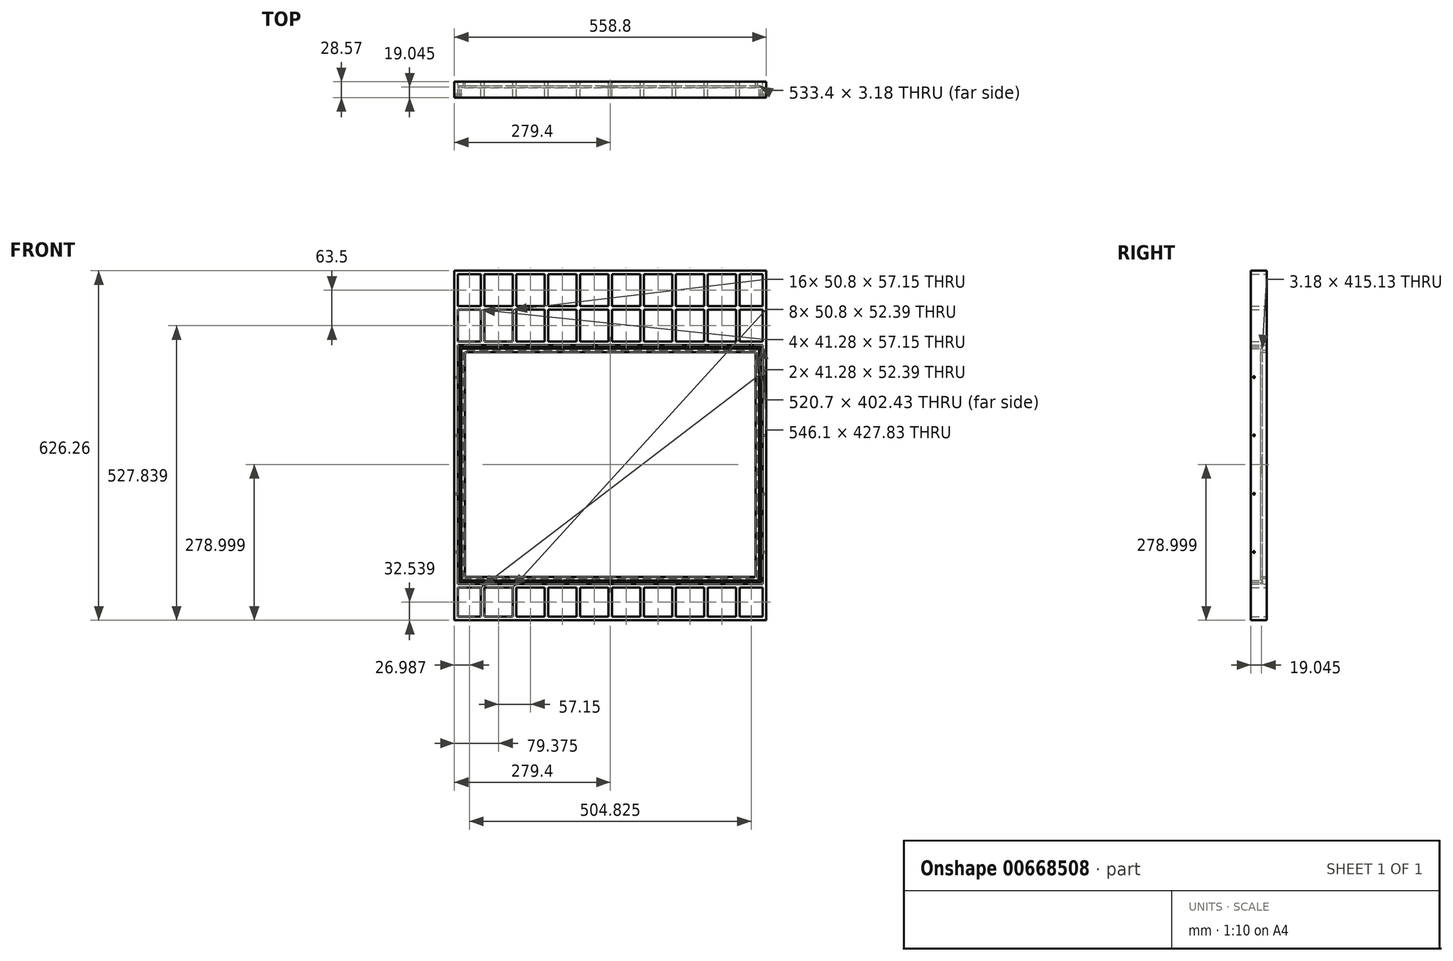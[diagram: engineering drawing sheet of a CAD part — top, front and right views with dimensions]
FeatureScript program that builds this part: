
annotation { "Feature Type Name" : "Feature", "Feature Type Description" : "" }
export const myFeature = defineFeature(function(context is Context, id is Id, definition is map)
    precondition{}
    {
        {
            var Q0;
            Q0=qCreatedBy(makeId("Front.planeOp"),FACE);
            var sketch = newSketch(context, id + "F0", { "sketchPlane" : qUnion([Q0])});
            skLineSegment(sketch, "E0.bottom", {"start": v(-279.4, -313.13) * mm, "end": v(279.4, -313.13) * mm});
            skLineSegment(sketch, "E0.top", {"start": v(-279.4, 313.13) * mm, "end": v(279.4, 313.13) * mm});
            skLineSegment(sketch, "E0.left", {"start": v(-279.4, -313.13) * mm, "end": v(-279.4, 313.13) * mm});
            skLineSegment(sketch, "E0.right", {"start": v(279.4, -313.13) * mm, "end": v(279.4, 313.13) * mm});
            skPoint(sketch, "E0.middle", {"position": v(0, 0) * mm});
            skLineSegment(sketch, "E1.0", {"start": v(-273.05, 179.78) * mm, "end": v(273.05, 179.78) * mm});
            skLineSegment(sketch, "E2", {"start": v(-409.08, -332.18) * mm, "end": v(546.13, -332.18) * mm, "construction": true});
            skLineSegment(sketch, "E3.0", {"start": v(-409.08, -351.23) * mm, "end": v(546.13, -351.23) * mm});
            skLineSegment(sketch, "E4", {"start": v(-273.05, -248.05) * mm, "end": v(273.05, -248.05) * mm});
            skLineSegment(sketch, "E5.0", {"start": v(-273.05, -306.78) * mm, "end": v(-273.05, 306.78) * mm});
            skLineSegment(sketch, "E5.1", {"start": v(-273.05, -306.78) * mm, "end": v(273.05, -306.78) * mm});
            skLineSegment(sketch, "E5.2", {"start": v(273.05, -306.78) * mm, "end": v(273.05, 306.78) * mm});
            skLineSegment(sketch, "E5.3", {"start": v(-273.05, 306.78) * mm, "end": v(273.05, 306.78) * mm});
            skLineSegment(sketch, "E6.0", {"start": v(-273.05, 186.13) * mm, "end": v(273.05, 186.13) * mm});
            skLineSegment(sketch, "E7", {"start": v(-291.57, 348.06) * mm, "end": v(292.45, 348.06) * mm, "construction": true});
            skLineSegment(sketch, "E8.0", {"start": v(-273.05, -254.4) * mm, "end": v(273.05, -254.4) * mm});
            skLineSegment(sketch, "E9", {"start": v(0, 186.13) * mm, "end": v(0, 306.78) * mm, "construction": true});
            skLineSegment(sketch, "E10", {"start": v(53.97, 306.78) * mm, "end": v(53.98, 186.13) * mm});
            skLineSegment(sketch, "E11", {"start": v(111.13, 306.78) * mm, "end": v(111.13, 186.13) * mm});
            skLineSegment(sketch, "E12", {"start": v(168.28, 306.78) * mm, "end": v(168.28, 186.13) * mm});
            skLineSegment(sketch, "E13.0", {"start": v(3.18, 186.13) * mm, "end": v(3.18, 306.78) * mm});
            skLineSegment(sketch, "E14.0", {"start": v(60.33, 306.78) * mm, "end": v(60.33, 186.13) * mm});
            skLineSegment(sketch, "E15", {"start": v(117.48, 306.78) * mm, "end": v(117.48, 186.13) * mm});
            skLineSegment(sketch, "E16", {"start": v(174.63, 306.78) * mm, "end": v(174.63, 186.13) * mm});
            skLineSegment(sketch, "E17.0", {"start": v(225.43, 306.78) * mm, "end": v(225.43, 186.13) * mm});
            skLineSegment(sketch, "E18.0", {"start": v(231.78, 313.13) * mm, "end": v(231.78, 186.13) * mm});
            skLineSegment(sketch, "E19.0", {"start": v(-3.18, 186.13) * mm, "end": v(-3.18, 306.78) * mm});
            skLineSegment(sketch, "E20.0", {"start": v(-53.98, 186.13) * mm, "end": v(-53.98, 306.78) * mm});
            skLineSegment(sketch, "E21.0", {"start": v(-60.33, 186.13) * mm, "end": v(-60.33, 306.78) * mm});
            skLineSegment(sketch, "E22.0", {"start": v(-111.12, 186.13) * mm, "end": v(-111.12, 306.78) * mm});
            skLineSegment(sketch, "E23.0", {"start": v(-117.47, 186.13) * mm, "end": v(-117.47, 306.78) * mm});
            skLineSegment(sketch, "E24.0", {"start": v(-168.28, 186.13) * mm, "end": v(-168.28, 306.78) * mm});
            skLineSegment(sketch, "E25.0", {"start": v(-174.62, 186.13) * mm, "end": v(-174.62, 306.78) * mm});
            skLineSegment(sketch, "E26.0", {"start": v(-225.42, 186.13) * mm, "end": v(-225.42, 306.78) * mm});
            skLineSegment(sketch, "E27.0", {"start": v(-231.78, 186.13) * mm, "end": v(-231.78, 306.78) * mm});
            skPoint(sketch, "E28.endSnap0", {"position": v(231.78, 249.63) * mm});
            skLineSegment(sketch, "E29", {"start": v(0, 246.46) * mm, "end": v(-273.05, 246.46) * mm, "construction": true});
            skLineSegment(sketch, "E30.0", {"start": v(273.05, 249.63) * mm, "end": v(-273.05, 249.63) * mm});
            skLineSegment(sketch, "E31.0", {"start": v(273.05, 243.28) * mm, "end": v(-273.05, 243.28) * mm});
            skLineSegment(sketch, "E32", {"start": v(-231.78, -248.05) * mm, "end": v(-231.78, -306.78) * mm});
            skLineSegment(sketch, "E33.0", {"start": v(-225.43, -254.4) * mm, "end": v(-225.43, -306.78) * mm});
            skLineSegment(sketch, "E34.0", {"start": v(-174.63, -254.4) * mm, "end": v(-174.63, -306.78) * mm});
            skLineSegment(sketch, "E35.0", {"start": v(-168.28, -254.4) * mm, "end": v(-168.28, -306.78) * mm});
            skLineSegment(sketch, "E36", {"start": v(-117.48, -254.4) * mm, "end": v(-117.48, -306.78) * mm});
            skLineSegment(sketch, "E37", {"start": v(-111.13, -254.4) * mm, "end": v(-111.13, -306.78) * mm});
            skLineSegment(sketch, "E38", {"start": v(-60.33, -254.4) * mm, "end": v(-60.33, -306.78) * mm});
            skLineSegment(sketch, "E39", {"start": v(-53.98, -254.4) * mm, "end": v(-53.98, -306.78) * mm});
            skLineSegment(sketch, "E40", {"start": v(-3.18, -254.4) * mm, "end": v(-3.18, -306.78) * mm});
            skLineSegment(sketch, "E41", {"start": v(3.17, -254.4) * mm, "end": v(3.17, -306.78) * mm});
            skLineSegment(sketch, "E42", {"start": v(53.97, -254.4) * mm, "end": v(53.97, -306.78) * mm});
            skLineSegment(sketch, "E43", {"start": v(60.32, -254.4) * mm, "end": v(60.32, -306.78) * mm});
            skLineSegment(sketch, "E44", {"start": v(111.12, -254.4) * mm, "end": v(111.12, -306.78) * mm});
            skLineSegment(sketch, "E45", {"start": v(117.47, -254.4) * mm, "end": v(117.47, -306.78) * mm});
            skLineSegment(sketch, "E46", {"start": v(168.27, -254.4) * mm, "end": v(168.27, -306.78) * mm});
            skLineSegment(sketch, "E47", {"start": v(174.62, -254.4) * mm, "end": v(174.62, -306.78) * mm});
            skLineSegment(sketch, "E48", {"start": v(225.42, -254.4) * mm, "end": v(225.42, -306.78) * mm});
            skLineSegment(sketch, "E49", {"start": v(231.77, -254.4) * mm, "end": v(231.77, -306.78) * mm});
            skSolve(sketch);
        }
        {
            var Q0;
            Q0 = qSketchRegion(id + "F0", true);
            var Q1;
            {var subQ0=sQuery(id+"F0.wireOp",EDGE,"E26.0");var subQ1=sQuery(id+"F0.wireOp",EDGE,"E5.3");var subQ2=makeQuery(id+"F0.imprint","INTERSECT",VERTEX,{"derivedFrom":[subQ1,subQ0]});Q1=makeQuery(id+"F0.imprint","IMPRINT",FACE,{"disambiguationData":[TD([[makeQuery(id+"F0.imprint","IMPRINT",EDGE,{"disambiguationData":[TD([[subQ2,1.0]])],"derivedFrom":subQ1}),-1.0]])]});}
            var Q2;
            {var subQ0=sQuery(id+"F0.wireOp",EDGE,"E31.0");var subQ1=sQuery(id+"F0.wireOp",EDGE,"E26.0");var subQ2=makeQuery(id+"F0.imprint","INTERSECT",VERTEX,{"derivedFrom":[subQ1,subQ0]});Q2=makeQuery(id+"F0.imprint","IMPRINT",FACE,{"disambiguationData":[TD([[makeQuery(id+"F0.imprint","IMPRINT",EDGE,{"disambiguationData":[TD([[subQ2,-1.0]])],"derivedFrom":subQ1}),1.0]])]});}
            var Q3;
            {var subQ0=sQuery(id+"F0.wireOp",EDGE,"E30.0");var subQ1=sQuery(id+"F0.wireOp",EDGE,"E5.0");var subQ2=makeQuery(id+"F0.imprint","INTERSECT",VERTEX,{"derivedFrom":[subQ1,subQ0]});Q3=makeQuery(id+"F0.imprint","IMPRINT",FACE,{"disambiguationData":[TD([[makeQuery(id+"F0.imprint","IMPRINT",EDGE,{"disambiguationData":[TD([[subQ2,1.0]])],"derivedFrom":subQ1}),-1.0]])]});}
            var Q4;
            {var subQ0=sQuery(id+"F0.wireOp",EDGE,"E26.0");var subQ1=sQuery(id+"F0.wireOp",EDGE,"E6.0");var subQ2=makeQuery(id+"F0.imprint","INTERSECT",VERTEX,{"derivedFrom":[subQ1,subQ0]});Q4=makeQuery(id+"F0.imprint","IMPRINT",FACE,{"disambiguationData":[TD([[makeQuery(id+"F0.imprint","IMPRINT",EDGE,{"disambiguationData":[TD([[subQ2,1.0]])],"derivedFrom":subQ1}),1.0]])]});}
            var Q5;
            {var subQ0=sQuery(id+"F0.wireOp",EDGE,"E31.0");var subQ1=sQuery(id+"F0.wireOp",EDGE,"E25.0");var subQ2=makeQuery(id+"F0.imprint","INTERSECT",VERTEX,{"derivedFrom":[subQ1,subQ0]});Q5=makeQuery(id+"F0.imprint","IMPRINT",FACE,{"disambiguationData":[TD([[makeQuery(id+"F0.imprint","IMPRINT",EDGE,{"disambiguationData":[TD([[subQ2,-1.0]])],"derivedFrom":subQ1}),1.0]])]});}
            var Q6;
            {var subQ0=sQuery(id+"F0.wireOp",EDGE,"E31.0");var subQ1=sQuery(id+"F0.wireOp",EDGE,"E24.0");var subQ2=makeQuery(id+"F0.imprint","INTERSECT",VERTEX,{"derivedFrom":[subQ1,subQ0]});Q6=makeQuery(id+"F0.imprint","IMPRINT",FACE,{"disambiguationData":[TD([[makeQuery(id+"F0.imprint","IMPRINT",EDGE,{"disambiguationData":[TD([[subQ2,-1.0]])],"derivedFrom":subQ1}),1.0]])]});}
            var Q7;
            {var subQ0=sQuery(id+"F0.wireOp",EDGE,"E24.0");var subQ1=sQuery(id+"F0.wireOp",EDGE,"E5.3");var subQ2=makeQuery(id+"F0.imprint","INTERSECT",VERTEX,{"derivedFrom":[subQ1,subQ0]});Q7=makeQuery(id+"F0.imprint","IMPRINT",FACE,{"disambiguationData":[TD([[makeQuery(id+"F0.imprint","IMPRINT",EDGE,{"disambiguationData":[TD([[subQ2,1.0]])],"derivedFrom":subQ1}),-1.0]])]});}
            var Q8;
            {var subQ0=sQuery(id+"F0.wireOp",EDGE,"E24.0");var subQ1=sQuery(id+"F0.wireOp",EDGE,"E6.0");var subQ2=makeQuery(id+"F0.imprint","INTERSECT",VERTEX,{"derivedFrom":[subQ1,subQ0]});Q8=makeQuery(id+"F0.imprint","IMPRINT",FACE,{"disambiguationData":[TD([[makeQuery(id+"F0.imprint","IMPRINT",EDGE,{"disambiguationData":[TD([[subQ2,1.0]])],"derivedFrom":subQ1}),1.0]])]});}
            var Q9;
            {var subQ0=sQuery(id+"F0.wireOp",EDGE,"E31.0");var subQ1=sQuery(id+"F0.wireOp",EDGE,"E23.0");var subQ2=makeQuery(id+"F0.imprint","INTERSECT",VERTEX,{"derivedFrom":[subQ1,subQ0]});Q9=makeQuery(id+"F0.imprint","IMPRINT",FACE,{"disambiguationData":[TD([[makeQuery(id+"F0.imprint","IMPRINT",EDGE,{"disambiguationData":[TD([[subQ2,-1.0]])],"derivedFrom":subQ1}),1.0]])]});}
            var Q10;
            {var subQ0=sQuery(id+"F0.wireOp",EDGE,"E22.0");var subQ1=sQuery(id+"F0.wireOp",EDGE,"E6.0");var subQ2=makeQuery(id+"F0.imprint","INTERSECT",VERTEX,{"derivedFrom":[subQ1,subQ0]});Q10=makeQuery(id+"F0.imprint","IMPRINT",FACE,{"disambiguationData":[TD([[makeQuery(id+"F0.imprint","IMPRINT",EDGE,{"disambiguationData":[TD([[subQ2,1.0]])],"derivedFrom":subQ1}),1.0]])]});}
            var Q11;
            {var subQ0=sQuery(id+"F0.wireOp",EDGE,"E31.0");var subQ1=sQuery(id+"F0.wireOp",EDGE,"E22.0");var subQ2=makeQuery(id+"F0.imprint","INTERSECT",VERTEX,{"derivedFrom":[subQ1,subQ0]});Q11=makeQuery(id+"F0.imprint","IMPRINT",FACE,{"disambiguationData":[TD([[makeQuery(id+"F0.imprint","IMPRINT",EDGE,{"disambiguationData":[TD([[subQ2,-1.0]])],"derivedFrom":subQ1}),1.0]])]});}
            var Q12;
            {var subQ0=sQuery(id+"F0.wireOp",EDGE,"E22.0");var subQ1=sQuery(id+"F0.wireOp",EDGE,"E5.3");var subQ2=makeQuery(id+"F0.imprint","INTERSECT",VERTEX,{"derivedFrom":[subQ1,subQ0]});Q12=makeQuery(id+"F0.imprint","IMPRINT",FACE,{"disambiguationData":[TD([[makeQuery(id+"F0.imprint","IMPRINT",EDGE,{"disambiguationData":[TD([[subQ2,1.0]])],"derivedFrom":subQ1}),-1.0]])]});}
            var Q13;
            {var subQ0=sQuery(id+"F0.wireOp",EDGE,"E31.0");var subQ1=sQuery(id+"F0.wireOp",EDGE,"E21.0");var subQ2=makeQuery(id+"F0.imprint","INTERSECT",VERTEX,{"derivedFrom":[subQ1,subQ0]});Q13=makeQuery(id+"F0.imprint","IMPRINT",FACE,{"disambiguationData":[TD([[makeQuery(id+"F0.imprint","IMPRINT",EDGE,{"disambiguationData":[TD([[subQ2,-1.0]])],"derivedFrom":subQ1}),1.0]])]});}
            var Q14;
            {var subQ0=sQuery(id+"F0.wireOp",EDGE,"E31.0");var subQ1=sQuery(id+"F0.wireOp",EDGE,"E20.0");var subQ2=makeQuery(id+"F0.imprint","INTERSECT",VERTEX,{"derivedFrom":[subQ1,subQ0]});Q14=makeQuery(id+"F0.imprint","IMPRINT",FACE,{"disambiguationData":[TD([[makeQuery(id+"F0.imprint","IMPRINT",EDGE,{"disambiguationData":[TD([[subQ2,-1.0]])],"derivedFrom":subQ1}),1.0]])]});}
            var Q15;
            {var subQ0=sQuery(id+"F0.wireOp",EDGE,"E20.0");var subQ1=sQuery(id+"F0.wireOp",EDGE,"E5.3");var subQ2=makeQuery(id+"F0.imprint","INTERSECT",VERTEX,{"derivedFrom":[subQ1,subQ0]});Q15=makeQuery(id+"F0.imprint","IMPRINT",FACE,{"disambiguationData":[TD([[makeQuery(id+"F0.imprint","IMPRINT",EDGE,{"disambiguationData":[TD([[subQ2,1.0]])],"derivedFrom":subQ1}),-1.0]])]});}
            var Q16;
            {var subQ0=sQuery(id+"F0.wireOp",EDGE,"E20.0");var subQ1=sQuery(id+"F0.wireOp",EDGE,"E6.0");var subQ2=makeQuery(id+"F0.imprint","INTERSECT",VERTEX,{"derivedFrom":[subQ1,subQ0]});Q16=makeQuery(id+"F0.imprint","IMPRINT",FACE,{"disambiguationData":[TD([[makeQuery(id+"F0.imprint","IMPRINT",EDGE,{"disambiguationData":[TD([[subQ2,1.0]])],"derivedFrom":subQ1}),1.0]])]});}
            var Q17;
            {var subQ7=sQuery(id+"F0.wireOp",EDGE,"E1.0");Q17=makeQuery(id+"F0.imprint","IMPRINT",FACE,{"disambiguationData":[TD([[makeQuery(id+"F0.imprint","IMPRINT",EDGE,{"derivedFrom":subQ7}),1.0]])]});}
            var Q18;
            {var subQ0=sQuery(id+"F0.wireOp",EDGE,"E13.0");var subQ1=sQuery(id+"F0.wireOp",EDGE,"E6.0");var subQ2=makeQuery(id+"F0.imprint","INTERSECT",VERTEX,{"derivedFrom":[subQ1,subQ0]});Q18=makeQuery(id+"F0.imprint","IMPRINT",FACE,{"disambiguationData":[TD([[makeQuery(id+"F0.imprint","IMPRINT",EDGE,{"disambiguationData":[TD([[subQ2,1.0]])],"derivedFrom":subQ1}),1.0]])]});}
            var Q19;
            {var subQ0=sQuery(id+"F0.wireOp",EDGE,"E31.0");var subQ1=sQuery(id+"F0.wireOp",EDGE,"E13.0");var subQ2=makeQuery(id+"F0.imprint","INTERSECT",VERTEX,{"derivedFrom":[subQ1,subQ0]});Q19=makeQuery(id+"F0.imprint","IMPRINT",FACE,{"disambiguationData":[TD([[makeQuery(id+"F0.imprint","IMPRINT",EDGE,{"disambiguationData":[TD([[subQ2,-1.0]])],"derivedFrom":subQ1}),1.0]])]});}
            var Q20;
            {var subQ0=sQuery(id+"F0.wireOp",EDGE,"E31.0");var subQ1=sQuery(id+"F0.wireOp",EDGE,"E19.0");var subQ2=makeQuery(id+"F0.imprint","INTERSECT",VERTEX,{"derivedFrom":[subQ1,subQ0]});Q20=makeQuery(id+"F0.imprint","IMPRINT",FACE,{"disambiguationData":[TD([[makeQuery(id+"F0.imprint","IMPRINT",EDGE,{"disambiguationData":[TD([[subQ2,-1.0]])],"derivedFrom":subQ1}),1.0]])]});}
            var Q21;
            {var subQ0=sQuery(id+"F0.wireOp",EDGE,"E13.0");var subQ1=sQuery(id+"F0.wireOp",EDGE,"E5.3");var subQ2=makeQuery(id+"F0.imprint","INTERSECT",VERTEX,{"derivedFrom":[subQ1,subQ0]});Q21=makeQuery(id+"F0.imprint","IMPRINT",FACE,{"disambiguationData":[TD([[makeQuery(id+"F0.imprint","IMPRINT",EDGE,{"disambiguationData":[TD([[subQ2,1.0]])],"derivedFrom":subQ1}),-1.0]])]});}
            var Q22;
            {var subQ0=sQuery(id+"F0.wireOp",EDGE,"E30.0");var subQ1=sQuery(id+"F0.wireOp",EDGE,"E10");var subQ2=makeQuery(id+"F0.imprint","INTERSECT",VERTEX,{"derivedFrom":[subQ1,subQ0]});Q22=makeQuery(id+"F0.imprint","IMPRINT",FACE,{"disambiguationData":[TD([[makeQuery(id+"F0.imprint","IMPRINT",EDGE,{"disambiguationData":[TD([[subQ2,-1.0]])],"derivedFrom":subQ1}),-1.0]])]});}
            var Q23;
            {var subQ0=sQuery(id+"F0.wireOp",EDGE,"E30.0");var subQ1=sQuery(id+"F0.wireOp",EDGE,"E10");var subQ2=makeQuery(id+"F0.imprint","INTERSECT",VERTEX,{"derivedFrom":[subQ1,subQ0]});Q23=makeQuery(id+"F0.imprint","IMPRINT",FACE,{"disambiguationData":[TD([[makeQuery(id+"F0.imprint","IMPRINT",EDGE,{"disambiguationData":[TD([[subQ2,-1.0]])],"derivedFrom":subQ1}),1.0]])]});}
            var Q24;
            {var subQ0=sQuery(id+"F0.wireOp",EDGE,"E10");var subQ1=sQuery(id+"F0.wireOp",EDGE,"E5.3");var subQ2=makeQuery(id+"F0.imprint","INTERSECT",VERTEX,{"derivedFrom":[subQ1,subQ0]});Q24=makeQuery(id+"F0.imprint","IMPRINT",FACE,{"disambiguationData":[TD([[makeQuery(id+"F0.imprint","IMPRINT",EDGE,{"disambiguationData":[TD([[subQ2,-1.0]])],"derivedFrom":subQ1}),-1.0]])]});}
            var Q25;
            {var subQ0=sQuery(id+"F0.wireOp",EDGE,"E10");var subQ1=sQuery(id+"F0.wireOp",EDGE,"E6.0");var subQ2=makeQuery(id+"F0.imprint","INTERSECT",VERTEX,{"derivedFrom":[subQ1,subQ0]});Q25=makeQuery(id+"F0.imprint","IMPRINT",FACE,{"disambiguationData":[TD([[makeQuery(id+"F0.imprint","IMPRINT",EDGE,{"disambiguationData":[TD([[subQ2,-1.0]])],"derivedFrom":subQ1}),1.0]])]});}
            var Q26;
            {var subQ0=sQuery(id+"F0.wireOp",EDGE,"E30.0");var subQ1=sQuery(id+"F0.wireOp",EDGE,"E11");var subQ2=makeQuery(id+"F0.imprint","INTERSECT",VERTEX,{"derivedFrom":[subQ1,subQ0]});Q26=makeQuery(id+"F0.imprint","IMPRINT",FACE,{"disambiguationData":[TD([[makeQuery(id+"F0.imprint","IMPRINT",EDGE,{"disambiguationData":[TD([[subQ2,-1.0]])],"derivedFrom":subQ1}),-1.0]])]});}
            var Q27;
            {var subQ0=sQuery(id+"F0.wireOp",EDGE,"E30.0");var subQ1=sQuery(id+"F0.wireOp",EDGE,"E11");var subQ2=makeQuery(id+"F0.imprint","INTERSECT",VERTEX,{"derivedFrom":[subQ1,subQ0]});Q27=makeQuery(id+"F0.imprint","IMPRINT",FACE,{"disambiguationData":[TD([[makeQuery(id+"F0.imprint","IMPRINT",EDGE,{"disambiguationData":[TD([[subQ2,-1.0]])],"derivedFrom":subQ1}),1.0]])]});}
            var Q28;
            {var subQ0=sQuery(id+"F0.wireOp",EDGE,"E11");var subQ1=sQuery(id+"F0.wireOp",EDGE,"E6.0");var subQ2=makeQuery(id+"F0.imprint","INTERSECT",VERTEX,{"derivedFrom":[subQ1,subQ0]});Q28=makeQuery(id+"F0.imprint","IMPRINT",FACE,{"disambiguationData":[TD([[makeQuery(id+"F0.imprint","IMPRINT",EDGE,{"disambiguationData":[TD([[subQ2,-1.0]])],"derivedFrom":subQ1}),1.0]])]});}
            var Q29;
            {var subQ0=sQuery(id+"F0.wireOp",EDGE,"E11");var subQ1=sQuery(id+"F0.wireOp",EDGE,"E5.3");var subQ2=makeQuery(id+"F0.imprint","INTERSECT",VERTEX,{"derivedFrom":[subQ1,subQ0]});Q29=makeQuery(id+"F0.imprint","IMPRINT",FACE,{"disambiguationData":[TD([[makeQuery(id+"F0.imprint","IMPRINT",EDGE,{"disambiguationData":[TD([[subQ2,-1.0]])],"derivedFrom":subQ1}),-1.0]])]});}
            var Q30;
            {var subQ0=sQuery(id+"F0.wireOp",EDGE,"E30.0");var subQ1=sQuery(id+"F0.wireOp",EDGE,"E12");var subQ2=makeQuery(id+"F0.imprint","INTERSECT",VERTEX,{"derivedFrom":[subQ1,subQ0]});Q30=makeQuery(id+"F0.imprint","IMPRINT",FACE,{"disambiguationData":[TD([[makeQuery(id+"F0.imprint","IMPRINT",EDGE,{"disambiguationData":[TD([[subQ2,-1.0]])],"derivedFrom":subQ1}),-1.0]])]});}
            var Q31;
            {var subQ0=sQuery(id+"F0.wireOp",EDGE,"E12");var subQ1=sQuery(id+"F0.wireOp",EDGE,"E5.3");var subQ2=makeQuery(id+"F0.imprint","INTERSECT",VERTEX,{"derivedFrom":[subQ1,subQ0]});Q31=makeQuery(id+"F0.imprint","IMPRINT",FACE,{"disambiguationData":[TD([[makeQuery(id+"F0.imprint","IMPRINT",EDGE,{"disambiguationData":[TD([[subQ2,-1.0]])],"derivedFrom":subQ1}),-1.0]])]});}
            var Q32;
            {var subQ0=sQuery(id+"F0.wireOp",EDGE,"E30.0");var subQ1=sQuery(id+"F0.wireOp",EDGE,"E12");var subQ2=makeQuery(id+"F0.imprint","INTERSECT",VERTEX,{"derivedFrom":[subQ1,subQ0]});Q32=makeQuery(id+"F0.imprint","IMPRINT",FACE,{"disambiguationData":[TD([[makeQuery(id+"F0.imprint","IMPRINT",EDGE,{"disambiguationData":[TD([[subQ2,-1.0]])],"derivedFrom":subQ1}),1.0]])]});}
            var Q33;
            {var subQ0=sQuery(id+"F0.wireOp",EDGE,"E12");var subQ1=sQuery(id+"F0.wireOp",EDGE,"E6.0");var subQ2=makeQuery(id+"F0.imprint","INTERSECT",VERTEX,{"derivedFrom":[subQ1,subQ0]});Q33=makeQuery(id+"F0.imprint","IMPRINT",FACE,{"disambiguationData":[TD([[makeQuery(id+"F0.imprint","IMPRINT",EDGE,{"disambiguationData":[TD([[subQ2,-1.0]])],"derivedFrom":subQ1}),1.0]])]});}
            var Q34;
            {var subQ0=sQuery(id+"F0.wireOp",EDGE,"E30.0");var subQ1=sQuery(id+"F0.wireOp",EDGE,"E16");var subQ2=makeQuery(id+"F0.imprint","INTERSECT",VERTEX,{"derivedFrom":[subQ1,subQ0]});Q34=makeQuery(id+"F0.imprint","IMPRINT",FACE,{"disambiguationData":[TD([[makeQuery(id+"F0.imprint","IMPRINT",EDGE,{"disambiguationData":[TD([[subQ2,-1.0]])],"derivedFrom":subQ1}),1.0]])]});}
            var Q35;
            {var subQ0=sQuery(id+"F0.wireOp",EDGE,"E17.0");var subQ1=sQuery(id+"F0.wireOp",EDGE,"E6.0");var subQ2=makeQuery(id+"F0.imprint","INTERSECT",VERTEX,{"derivedFrom":[subQ1,subQ0]});Q35=makeQuery(id+"F0.imprint","IMPRINT",FACE,{"disambiguationData":[TD([[makeQuery(id+"F0.imprint","IMPRINT",EDGE,{"disambiguationData":[TD([[subQ2,-1.0]])],"derivedFrom":subQ1}),1.0]])]});}
            var Q36;
            {var subQ0=sQuery(id+"F0.wireOp",EDGE,"E30.0");var subQ1=sQuery(id+"F0.wireOp",EDGE,"E17.0");var subQ2=makeQuery(id+"F0.imprint","INTERSECT",VERTEX,{"derivedFrom":[subQ1,subQ0]});Q36=makeQuery(id+"F0.imprint","IMPRINT",FACE,{"disambiguationData":[TD([[makeQuery(id+"F0.imprint","IMPRINT",EDGE,{"disambiguationData":[TD([[subQ2,-1.0]])],"derivedFrom":subQ1}),1.0]])]});}
            var Q37;
            {var subQ0=sQuery(id+"F0.wireOp",EDGE,"E17.0");var subQ1=sQuery(id+"F0.wireOp",EDGE,"E5.3");var subQ2=makeQuery(id+"F0.imprint","INTERSECT",VERTEX,{"derivedFrom":[subQ1,subQ0]});Q37=makeQuery(id+"F0.imprint","IMPRINT",FACE,{"disambiguationData":[TD([[makeQuery(id+"F0.imprint","IMPRINT",EDGE,{"disambiguationData":[TD([[subQ2,-1.0]])],"derivedFrom":subQ1}),-1.0]])]});}
            var Q38;
            {var subQ0=sQuery(id+"F0.wireOp",EDGE,"E30.0");var subQ1=sQuery(id+"F0.wireOp",EDGE,"E5.2");var subQ2=makeQuery(id+"F0.imprint","INTERSECT",VERTEX,{"derivedFrom":[subQ1,subQ0]});Q38=makeQuery(id+"F0.imprint","IMPRINT",FACE,{"disambiguationData":[TD([[makeQuery(id+"F0.imprint","IMPRINT",EDGE,{"disambiguationData":[TD([[subQ2,1.0]])],"derivedFrom":subQ1}),1.0]])]});}
            var Q39;
            {var subQ8=sQuery(id+"F0.wireOp",EDGE,"E5.2");var subQ9=sQuery(id+"F0.wireOp",EDGE,"E4");var subQ10=makeQuery(id+"F0.imprint","INTERSECT",VERTEX,{"derivedFrom":[subQ9,subQ8]});Q39=makeQuery(id+"F0.imprint","IMPRINT",FACE,{"disambiguationData":[TD([[makeQuery(id+"F0.imprint","IMPRINT",EDGE,{"disambiguationData":[TD([[subQ10,1.0]])],"derivedFrom":subQ9}),-1.0]])]});}
            var Q40;
            {var subQ0=sQuery(id+"F0.wireOp",EDGE,"E38");Q40=makeQuery(id+"F0.imprint","IMPRINT",FACE,{"disambiguationData":[TD([[makeQuery(id+"F0.imprint","IMPRINT",EDGE,{"derivedFrom":subQ0}),1.0]])]});}
            var Q41;
            {var subQ0=sQuery(id+"F0.wireOp",EDGE,"E36");Q41=makeQuery(id+"F0.imprint","IMPRINT",FACE,{"disambiguationData":[TD([[makeQuery(id+"F0.imprint","IMPRINT",EDGE,{"derivedFrom":subQ0}),1.0]])]});}
            var Q42;
            {var subQ0=sQuery(id+"F0.wireOp",EDGE,"E34.0");Q42=makeQuery(id+"F0.imprint","IMPRINT",FACE,{"disambiguationData":[TD([[makeQuery(id+"F0.imprint","IMPRINT",EDGE,{"derivedFrom":subQ0}),1.0]])]});}
            var Q43;
            {var subQ3=sQuery(id+"F0.wireOp",EDGE,"E33.0");Q43=makeQuery(id+"F0.imprint","IMPRINT",FACE,{"disambiguationData":[TD([[makeQuery(id+"F0.imprint","IMPRINT",EDGE,{"derivedFrom":subQ3}),-1.0]])]});}
            var Q44;
            {var subQ0=sQuery(id+"F0.wireOp",EDGE,"E40");Q44=makeQuery(id+"F0.imprint","IMPRINT",FACE,{"disambiguationData":[TD([[makeQuery(id+"F0.imprint","IMPRINT",EDGE,{"derivedFrom":subQ0}),1.0]])]});}
            var Q45;
            {var subQ0=sQuery(id+"F0.wireOp",EDGE,"E42");Q45=makeQuery(id+"F0.imprint","IMPRINT",FACE,{"disambiguationData":[TD([[makeQuery(id+"F0.imprint","IMPRINT",EDGE,{"derivedFrom":subQ0}),1.0]])]});}
            var Q46;
            {var subQ0=sQuery(id+"F0.wireOp",EDGE,"E46");Q46=makeQuery(id+"F0.imprint","IMPRINT",FACE,{"disambiguationData":[TD([[makeQuery(id+"F0.imprint","IMPRINT",EDGE,{"derivedFrom":subQ0}),1.0]])]});}
            var Q47;
            {var subQ0=sQuery(id+"F0.wireOp",EDGE,"E5.0");var subQ1=sQuery(id+"F0.wireOp",EDGE,"E4");var subQ2=makeQuery(id+"F0.imprint","INTERSECT",VERTEX,{"derivedFrom":[subQ1,subQ0]});Q47=makeQuery(id+"F0.imprint","IMPRINT",FACE,{"disambiguationData":[TD([[makeQuery(id+"F0.imprint","IMPRINT",EDGE,{"disambiguationData":[TD([[subQ2,-1.0]])],"derivedFrom":subQ1}),-1.0]])]});}
            var Q48;
            {var subQ0=sQuery(id+"F0.wireOp",EDGE,"E44");Q48=makeQuery(id+"F0.imprint","IMPRINT",FACE,{"disambiguationData":[TD([[makeQuery(id+"F0.imprint","IMPRINT",EDGE,{"derivedFrom":subQ0}),1.0]])]});}
            var Q49;
            {var subQ0=sQuery(id+"F0.wireOp",EDGE,"E48");Q49=makeQuery(id+"F0.imprint","IMPRINT",FACE,{"disambiguationData":[TD([[makeQuery(id+"F0.imprint","IMPRINT",EDGE,{"derivedFrom":subQ0}),1.0]])]});}
            extrude(context, id + "F1", {"entities" : qUnion([Q0, Q1, Q2, Q3, Q4, Q5, Q6, Q7, Q8, Q9, Q10, Q11, Q12, Q13, Q14, Q15, Q16, Q17, Q18, Q19, Q20, Q21, Q22, Q23, Q24, Q25, Q26, Q27, Q28, Q29, Q30, Q31, Q32, Q33, Q34, Q35, Q36, Q37, Q38, Q39, Q40, Q41, Q42, Q43, Q44, Q45, Q46, Q47, Q48, Q49]), "depth" : 28.57 * mm, "offsetDistance" : 25.4 * mm});
        }
        {
            var Q0;
            {var subQ0=sQuery(id+"F0.wireOp",EDGE,"E5.0");Q0=makeQuery(id+"F1.opExtrude","SWEPT_FACE",FACE,{"disambiguationData":[OSD([subQ0]),TDD([makeQuery(id+"F0.imprint","IMPRINT",EDGE,{"disambiguationData":[TD([[makeQuery(id+"F0.imprint","INTERSECT",VERTEX,{"derivedFrom":[sQuery(id+"F0.wireOp",EDGE,"E1.0"),subQ0]}),1.0]])],"derivedFrom":subQ0})])]});}
            var sketch = newSketch(context, id + "F2", { "sketchPlane" : qUnion([Q0])});
            skLineSegment(sketch, "E50.bottom", {"start": v(-7.94, -248.05) * mm, "end": v(-11.11, -248.05) * mm});
            skLineSegment(sketch, "E50.top", {"start": v(-7.94, 179.78) * mm, "end": v(-11.11, 179.78) * mm});
            skLineSegment(sketch, "E50.left", {"start": v(-7.94, -248.05) * mm, "end": v(-7.94, 179.78) * mm});
            skLineSegment(sketch, "E50.right", {"start": v(-11.11, -248.05) * mm, "end": v(-11.11, 179.78) * mm});
            skSolve(sketch);
        }
        {
            var Q0;
            Q0=makeQuery(id+"F1.opExtrude","SWEPT_FACE",FACE,{"disambiguationData":[OSD([sQuery(id+"F0.wireOp",EDGE,"E4")])]});
            var sketch = newSketch(context, id + "F3", { "sketchPlane" : qUnion([Q0])});
            skPoint(sketch, "E51.0", {"position": v(-273.05, -7.94) * mm});
            skPoint(sketch, "E52.0", {"position": v(-273.05, -11.11) * mm});
            skLineSegment(sketch, "E53.bottom", {"start": v(-273.05, -11.11) * mm, "end": v(273.05, -11.11) * mm});
            skLineSegment(sketch, "E53.top", {"start": v(-273.05, -7.94) * mm, "end": v(273.05, -7.94) * mm});
            skLineSegment(sketch, "E53.left", {"start": v(-273.05, -11.11) * mm, "end": v(-273.05, -7.94) * mm});
            skLineSegment(sketch, "E53.right", {"start": v(273.05, -11.11) * mm, "end": v(273.05, -7.94) * mm});
            skSolve(sketch);
        }
        {
            var Q0;
            {var subQ0=sQuery(id+"F0.wireOp",EDGE,"E5.2");Q0=makeQuery(id+"F1.opExtrude","SWEPT_FACE",FACE,{"disambiguationData":[OSD([subQ0]),TDD([makeQuery(id+"F0.imprint","IMPRINT",EDGE,{"disambiguationData":[TD([[makeQuery(id+"F0.imprint","INTERSECT",VERTEX,{"derivedFrom":[sQuery(id+"F0.wireOp",EDGE,"E1.0"),subQ0]}),1.0]])],"derivedFrom":subQ0})])]});}
            var sketch = newSketch(context, id + "F4", { "sketchPlane" : qUnion([Q0])});
            skPoint(sketch, "E54.0", {"position": v(7.94, -248.05) * mm});
            skPoint(sketch, "E55.0", {"position": v(11.11, -248.05) * mm});
            skLineSegment(sketch, "E56.bottom", {"start": v(7.94, -248.05) * mm, "end": v(11.11, -248.05) * mm});
            skLineSegment(sketch, "E56.top", {"start": v(7.94, 179.78) * mm, "end": v(11.11, 179.78) * mm});
            skLineSegment(sketch, "E56.left", {"start": v(7.94, -248.05) * mm, "end": v(7.94, 179.78) * mm});
            skLineSegment(sketch, "E56.right", {"start": v(11.11, -248.05) * mm, "end": v(11.11, 179.78) * mm});
            skSolve(sketch);
        }
        {
            var Q0;
            Q0=makeQuery(id+"F1.opExtrude","SWEPT_FACE",FACE,{"disambiguationData":[OSD([sQuery(id+"F0.wireOp",EDGE,"E1.0")])]});
            var sketch = newSketch(context, id + "F5", { "sketchPlane" : qUnion([Q0])});
            skPoint(sketch, "E57.0", {"position": v(273.05, 7.94) * mm});
            skPoint(sketch, "E58.0", {"position": v(273.05, 11.11) * mm});
            skLineSegment(sketch, "E59.bottom", {"start": v(273.05, 7.94) * mm, "end": v(-273.05, 7.94) * mm});
            skLineSegment(sketch, "E59.top", {"start": v(273.05, 11.11) * mm, "end": v(-273.05, 11.11) * mm});
            skLineSegment(sketch, "E59.left", {"start": v(273.05, 7.94) * mm, "end": v(273.05, 11.11) * mm});
            skLineSegment(sketch, "E59.right", {"start": v(-273.05, 7.94) * mm, "end": v(-273.05, 11.11) * mm});
            skSolve(sketch);
        }
        {
            var Q0;
            Q0=makeQuery(id+"F5.imprint","IMPRINT",FACE,{"disambiguationData":[TD([[makeQuery(id+"F5.imprint","IMPRINT",EDGE,{"derivedFrom":sQuery(id+"F5.wireOp",EDGE,"E59.bottom")}),-1.0]])]});
            extrude(context, id + "F6", {"entities" : qUnion([Q0]), "operationType" : NewBodyOperationType.ADD, "depth" : 12.7 * mm, "offsetDistance" : 25.4 * mm});
        }
        {
            var Q0;
            Q0=makeQuery(id+"F2.imprint","IMPRINT",FACE,{"disambiguationData":[TD([[makeQuery(id+"F2.imprint","IMPRINT",EDGE,{"derivedFrom":sQuery(id+"F2.wireOp",EDGE,"E50.bottom")}),1.0]])]});
            extrude(context, id + "F7", {"entities" : qUnion([Q0]), "operationType" : NewBodyOperationType.ADD, "depth" : 12.7 * mm, "offsetDistance" : 25.4 * mm});
        }
        {
            var Q0;
            Q0=makeQuery(id+"F3.imprint","IMPRINT",FACE,{"disambiguationData":[TD([[makeQuery(id+"F3.imprint","IMPRINT",EDGE,{"derivedFrom":sQuery(id+"F3.wireOp",EDGE,"E53.bottom")}),1.0]])]});
            extrude(context, id + "F8", {"entities" : qUnion([Q0]), "operationType" : NewBodyOperationType.ADD, "depth" : 12.7 * mm, "offsetDistance" : 25.4 * mm});
        }
        {
            var Q0;
            Q0=makeQuery(id+"F4.imprint","IMPRINT",FACE,{"disambiguationData":[TD([[makeQuery(id+"F4.imprint","IMPRINT",EDGE,{"derivedFrom":sQuery(id+"F4.wireOp",EDGE,"E56.bottom")}),-1.0]])]});
            extrude(context, id + "F9", {"entities" : qUnion([Q0]), "operationType" : NewBodyOperationType.ADD, "depth" : 12.7 * mm, "offsetDistance" : 25.4 * mm});
        }
        {
            var Q0;
            Q0=makeQuery(id+"F9.boolean.opBoolean","MERGE",FACE,{"derivedFrom":[makeQuery(id+"F8.boolean.opBoolean","MERGE",FACE,{"derivedFrom":[makeQuery(id+"F7.boolean.opBoolean","MERGE",FACE,{"derivedFrom":[makeQuery(id+"F6.opExtrude","SWEPT_FACE",FACE,{"disambiguationData":[OSD([sQuery(id+"F5.wireOp",EDGE,"E59.bottom")])]}),makeQuery(id+"F7.opExtrude","SWEPT_FACE",FACE,{"disambiguationData":[OSD([sQuery(id+"F2.wireOp",EDGE,"E50.left")])]})]}),makeQuery(id+"F8.opExtrude","SWEPT_FACE",FACE,{"disambiguationData":[OSD([sQuery(id+"F3.wireOp",EDGE,"E53.top")])]})]}),makeQuery(id+"F9.opExtrude","SWEPT_FACE",FACE,{"disambiguationData":[OSD([sQuery(id+"F4.wireOp",EDGE,"E56.left")])]})]});
            var sketch = newSketch(context, id + "F10", { "sketchPlane" : qUnion([Q0])});
            skLineSegment(sketch, "E60.0", {"start": v(-263.52, 170.26) * mm, "end": v(263.53, 170.26) * mm});
            skLineSegment(sketch, "E60.1", {"start": v(-263.53, -238.52) * mm, "end": v(-263.52, 170.26) * mm});
            skLineSegment(sketch, "E60.2", {"start": v(263.52, -238.52) * mm, "end": v(-263.53, -238.52) * mm});
            skLineSegment(sketch, "E60.3", {"start": v(263.52, -238.52) * mm, "end": v(263.53, 170.26) * mm});
            skSolve(sketch);
        }
        {
            var Q0;
            Q0=makeQuery(id+"F10.imprint","IMPRINT",FACE,{"disambiguationData":[TD([[makeQuery(id+"F10.imprint","IMPRINT",EDGE,{"derivedFrom":sQuery(id+"F10.wireOp",EDGE,"E60.0")}),-1.0]])]});
            extrude(context, id + "F11", {"entities" : qUnion([Q0]), "operationType" : NewBodyOperationType.ADD, "depth" : 7.94 * mm, "offsetDistance" : 25.4 * mm});
        }
        {
            var Q0;
            Q0=makeQuery(id+"F9.boolean.opBoolean","MERGE",FACE,{"derivedFrom":[makeQuery(id+"F8.boolean.opBoolean","MERGE",FACE,{"derivedFrom":[makeQuery(id+"F7.boolean.opBoolean","MERGE",FACE,{"derivedFrom":[makeQuery(id+"F6.opExtrude","SWEPT_FACE",FACE,{"disambiguationData":[OSD([sQuery(id+"F5.wireOp",EDGE,"E59.top")])]}),makeQuery(id+"F7.opExtrude","SWEPT_FACE",FACE,{"disambiguationData":[OSD([sQuery(id+"F2.wireOp",EDGE,"E50.right")])]})]}),makeQuery(id+"F8.opExtrude","SWEPT_FACE",FACE,{"disambiguationData":[OSD([sQuery(id+"F3.wireOp",EDGE,"E53.bottom")])]})]}),makeQuery(id+"F9.opExtrude","SWEPT_FACE",FACE,{"disambiguationData":[OSD([sQuery(id+"F4.wireOp",EDGE,"E56.right")])]})]});
            var sketch = newSketch(context, id + "F12", { "sketchPlane" : qUnion([Q0])});
            skLineSegment(sketch, "E61.bottom", {"start": v(-273.05, -248.05) * mm, "end": v(-266.7, -248.05) * mm});
            skLineSegment(sketch, "E61.top", {"start": v(-273.05, -241.7) * mm, "end": v(-266.7, -241.7) * mm});
            skLineSegment(sketch, "E61.left", {"start": v(-273.05, -248.05) * mm, "end": v(-273.05, -241.7) * mm});
            skLineSegment(sketch, "E61.right", {"start": v(-266.7, -248.05) * mm, "end": v(-266.7, -241.7) * mm});
            skLineSegment(sketch, "E62.bottom", {"start": v(273.05, -248.05) * mm, "end": v(266.7, -248.05) * mm});
            skLineSegment(sketch, "E62.top", {"start": v(273.05, -241.7) * mm, "end": v(266.7, -241.7) * mm});
            skLineSegment(sketch, "E62.left", {"start": v(273.05, -248.05) * mm, "end": v(273.05, -241.7) * mm});
            skLineSegment(sketch, "E62.right", {"start": v(266.7, -248.05) * mm, "end": v(266.7, -241.7) * mm});
            skLineSegment(sketch, "E63.bottom", {"start": v(-273.05, 179.78) * mm, "end": v(-266.7, 179.78) * mm});
            skLineSegment(sketch, "E63.top", {"start": v(-273.05, 173.43) * mm, "end": v(-266.7, 173.43) * mm});
            skLineSegment(sketch, "E63.left", {"start": v(-273.05, 179.78) * mm, "end": v(-273.05, 173.43) * mm});
            skLineSegment(sketch, "E63.right", {"start": v(-266.7, 179.78) * mm, "end": v(-266.7, 173.43) * mm});
            skLineSegment(sketch, "E64.bottom", {"start": v(273.05, 179.78) * mm, "end": v(266.7, 179.78) * mm});
            skLineSegment(sketch, "E64.top", {"start": v(273.05, 173.43) * mm, "end": v(266.7, 173.43) * mm});
            skLineSegment(sketch, "E64.left", {"start": v(273.05, 179.78) * mm, "end": v(273.05, 173.43) * mm});
            skLineSegment(sketch, "E64.right", {"start": v(266.7, 179.78) * mm, "end": v(266.7, 173.43) * mm});
            skSolve(sketch);
        }
        {
            var Q0;
            Q0 = qSketchRegion(id + "F12", true);
            extrude(context, id + "F13", {"entities" : qUnion([Q0]), "operationType" : NewBodyOperationType.REMOVE, "oppositeDirection" : true, "depth" : 25.4 * mm, "offsetDistance" : 25.4 * mm});
        }
        {
            var Q0;
            Q0=makeQuery(id+"F9.boolean.opBoolean","MERGE",FACE,{"derivedFrom":[makeQuery(id+"F8.boolean.opBoolean","MERGE",FACE,{"derivedFrom":[makeQuery(id+"F7.boolean.opBoolean","MERGE",FACE,{"derivedFrom":[makeQuery(id+"F6.opExtrude","SWEPT_FACE",FACE,{"disambiguationData":[OSD([sQuery(id+"F5.wireOp",EDGE,"E59.top")])]}),makeQuery(id+"F7.opExtrude","SWEPT_FACE",FACE,{"disambiguationData":[OSD([sQuery(id+"F2.wireOp",EDGE,"E50.right")])]})]}),makeQuery(id+"F8.opExtrude","SWEPT_FACE",FACE,{"disambiguationData":[OSD([sQuery(id+"F3.wireOp",EDGE,"E53.bottom")])]})]}),makeQuery(id+"F9.opExtrude","SWEPT_FACE",FACE,{"disambiguationData":[OSD([sQuery(id+"F4.wireOp",EDGE,"E56.right")])]})]});
            var sketch = newSketch(context, id + "F14", { "sketchPlane" : qUnion([Q0])});
            skLineSegment(sketch, "E65.bottom", {"start": v(-266.7, 173.43) * mm, "end": v(-269.88, 173.43) * mm});
            skLineSegment(sketch, "E65.top", {"start": v(-266.7, -241.7) * mm, "end": v(-269.88, -241.7) * mm});
            skLineSegment(sketch, "E65.left", {"start": v(-266.7, 173.43) * mm, "end": v(-266.7, -241.7) * mm});
            skLineSegment(sketch, "E65.right", {"start": v(-269.88, 173.43) * mm, "end": v(-269.88, -241.7) * mm});
            skLineSegment(sketch, "E66.bottom", {"start": v(-266.7, -241.7) * mm, "end": v(266.7, -241.7) * mm});
            skLineSegment(sketch, "E66.top", {"start": v(-266.7, -244.87) * mm, "end": v(266.7, -244.87) * mm});
            skLineSegment(sketch, "E66.left", {"start": v(-266.7, -241.7) * mm, "end": v(-266.7, -244.87) * mm});
            skLineSegment(sketch, "E66.right", {"start": v(266.7, -241.7) * mm, "end": v(266.7, -244.87) * mm});
            skLineSegment(sketch, "E67.bottom", {"start": v(266.7, -241.7) * mm, "end": v(269.88, -241.7) * mm});
            skLineSegment(sketch, "E67.top", {"start": v(266.7, 173.43) * mm, "end": v(269.88, 173.43) * mm});
            skLineSegment(sketch, "E67.left", {"start": v(266.7, -241.7) * mm, "end": v(266.7, 173.43) * mm});
            skLineSegment(sketch, "E67.right", {"start": v(269.88, -241.7) * mm, "end": v(269.88, 173.43) * mm});
            skLineSegment(sketch, "E68.bottom", {"start": v(266.7, 173.43) * mm, "end": v(-266.7, 173.43) * mm});
            skLineSegment(sketch, "E68.top", {"start": v(266.7, 176.6) * mm, "end": v(-266.7, 176.6) * mm});
            skLineSegment(sketch, "E68.left", {"start": v(266.7, 173.43) * mm, "end": v(266.7, 176.6) * mm});
            skLineSegment(sketch, "E68.right", {"start": v(-266.7, 173.43) * mm, "end": v(-266.7, 176.6) * mm});
            skLineSegment(sketch, "E69", {"start": v(-269.88, 173.43) * mm, "end": v(-269.88, 176.6) * mm});
            skLineSegment(sketch, "E70", {"start": v(-269.88, 176.6) * mm, "end": v(-266.7, 176.6) * mm});
            skLineSegment(sketch, "E71", {"start": v(-269.88, 176.6) * mm, "end": v(-273.05, 176.6) * mm});
            skLineSegment(sketch, "E72", {"start": v(-273.05, 176.6) * mm, "end": v(-273.05, 173.43) * mm});
            skLineSegment(sketch, "E73", {"start": v(-273.05, 173.43) * mm, "end": v(-269.88, 173.43) * mm});
            skLineSegment(sketch, "E74", {"start": v(-269.88, 176.6) * mm, "end": v(-269.88, 179.78) * mm});
            skLineSegment(sketch, "E75", {"start": v(-269.88, 179.78) * mm, "end": v(-266.7, 179.78) * mm});
            skLineSegment(sketch, "E76", {"start": v(-266.7, 179.78) * mm, "end": v(-266.7, 176.6) * mm});
            skLineSegment(sketch, "E77", {"start": v(266.7, 179.78) * mm, "end": v(269.88, 179.78) * mm});
            skLineSegment(sketch, "E78", {"start": v(269.88, 179.78) * mm, "end": v(269.88, 176.6) * mm});
            skLineSegment(sketch, "E79", {"start": v(269.88, 176.6) * mm, "end": v(273.05, 176.6) * mm});
            skLineSegment(sketch, "E80", {"start": v(273.05, 176.6) * mm, "end": v(273.05, 173.43) * mm});
            skLineSegment(sketch, "E81", {"start": v(266.7, 176.6) * mm, "end": v(269.88, 176.6) * mm});
            skLineSegment(sketch, "E82", {"start": v(269.88, 173.43) * mm, "end": v(269.88, 176.6) * mm});
            skLineSegment(sketch, "E83", {"start": v(266.7, -244.87) * mm, "end": v(269.88, -244.87) * mm});
            skLineSegment(sketch, "E84", {"start": v(269.88, -244.87) * mm, "end": v(269.88, -241.7) * mm});
            skLineSegment(sketch, "E85", {"start": v(273.05, -241.7) * mm, "end": v(273.05, -248.05) * mm});
            skLineSegment(sketch, "E86", {"start": v(273.05, -248.05) * mm, "end": v(266.7, -248.05) * mm});
            skLineSegment(sketch, "E87", {"start": v(266.7, -248.05) * mm, "end": v(266.7, -244.87) * mm});
            skLineSegment(sketch, "E88", {"start": v(269.88, -241.7) * mm, "end": v(273.05, -241.7) * mm});
            skLineSegment(sketch, "E89", {"start": v(-269.88, -241.7) * mm, "end": v(-269.88, -244.87) * mm});
            skLineSegment(sketch, "E90", {"start": v(-269.88, -244.87) * mm, "end": v(-266.7, -244.87) * mm});
            skLineSegment(sketch, "E91", {"start": v(-273.05, -241.7) * mm, "end": v(-269.88, -241.7) * mm});
            skLineSegment(sketch, "E92", {"start": v(-273.05, -241.7) * mm, "end": v(-273.05, -248.05) * mm});
            skLineSegment(sketch, "E93", {"start": v(-273.05, -248.05) * mm, "end": v(-266.7, -248.05) * mm});
            skLineSegment(sketch, "E94", {"start": v(-266.7, -248.05) * mm, "end": v(-266.7, -244.87) * mm});
            skLineSegment(sketch, "E95", {"start": v(-269.88, -244.87) * mm, "end": v(-273.05, -244.87) * mm});
            skLineSegment(sketch, "E96", {"start": v(-273.05, -244.87) * mm, "end": v(-269.88, -244.87) * mm});
            skLineSegment(sketch, "E97", {"start": v(-269.88, -244.87) * mm, "end": v(-269.88, -248.05) * mm});
            skLineSegment(sketch, "E98", {"start": v(269.88, -248.05) * mm, "end": v(269.88, -244.87) * mm});
            skLineSegment(sketch, "E99", {"start": v(269.88, -244.87) * mm, "end": v(273.05, -244.87) * mm});
            skLineSegment(sketch, "E100", {"start": v(269.88, 173.43) * mm, "end": v(273.05, 173.43) * mm});
            skSolve(sketch);
        }
        {
            var Q0;
            Q0=makeQuery(id+"F14.imprint","IMPRINT",FACE,{"disambiguationData":[TD([[makeQuery(id+"F14.imprint","IMPRINT",EDGE,{"derivedFrom":sQuery(id+"F14.wireOp",EDGE,"E69")}),1.0]])]});
            var Q1;
            Q1=makeQuery(id+"F14.imprint","IMPRINT",FACE,{"disambiguationData":[TD([[makeQuery(id+"F14.imprint","IMPRINT",EDGE,{"derivedFrom":sQuery(id+"F14.wireOp",EDGE,"E70")}),1.0]])]});
            var Q2;
            Q2=makeQuery(id+"F14.imprint","IMPRINT",FACE,{"disambiguationData":[TD([[makeQuery(id+"F14.imprint","IMPRINT",EDGE,{"derivedFrom":sQuery(id+"F14.wireOp",EDGE,"E79")}),-1.0]])]});
            var Q3;
            Q3=makeQuery(id+"F14.imprint","IMPRINT",FACE,{"disambiguationData":[TD([[makeQuery(id+"F14.imprint","IMPRINT",EDGE,{"derivedFrom":sQuery(id+"F14.wireOp",EDGE,"E83")}),-1.0]])]});
            var Q4;
            Q4=makeQuery(id+"F14.imprint","IMPRINT",FACE,{"disambiguationData":[TD([[makeQuery(id+"F14.imprint","IMPRINT",EDGE,{"derivedFrom":sQuery(id+"F14.wireOp",EDGE,"E84")}),-1.0]])]});
            var Q5;
            Q5=makeQuery(id+"F14.imprint","IMPRINT",FACE,{"disambiguationData":[TD([[makeQuery(id+"F14.imprint","IMPRINT",EDGE,{"derivedFrom":sQuery(id+"F14.wireOp",EDGE,"E89")}),-1.0]])]});
            var Q6;
            Q6=makeQuery(id+"F14.imprint","IMPRINT",FACE,{"disambiguationData":[TD([[makeQuery(id+"F14.imprint","IMPRINT",EDGE,{"derivedFrom":sQuery(id+"F14.wireOp",EDGE,"E90")}),-1.0]])]});
            var Q7;
            Q7=makeQuery(id+"F14.imprint","IMPRINT",FACE,{"disambiguationData":[TD([[makeQuery(id+"F14.imprint","IMPRINT",EDGE,{"derivedFrom":sQuery(id+"F14.wireOp",EDGE,"E65.bottom")}),1.0]])]});
            var Q8;
            Q8=makeQuery(id+"F14.imprint","IMPRINT",FACE,{"disambiguationData":[TD([[makeQuery(id+"F14.imprint","IMPRINT",EDGE,{"derivedFrom":sQuery(id+"F14.wireOp",EDGE,"E65.top")}),-1.0]])]});
            var Q9;
            Q9=makeQuery(id+"F14.imprint","IMPRINT",FACE,{"disambiguationData":[TD([[makeQuery(id+"F14.imprint","IMPRINT",EDGE,{"derivedFrom":sQuery(id+"F14.wireOp",EDGE,"E66.right")}),-1.0]])]});
            var Q10;
            Q10=makeQuery(id+"F14.imprint","IMPRINT",FACE,{"disambiguationData":[TD([[makeQuery(id+"F14.imprint","IMPRINT",EDGE,{"derivedFrom":sQuery(id+"F14.wireOp",EDGE,"E67.top")}),-1.0]])]});
            extrude(context, id + "F15", {"entities" : qUnion([Q0, Q1, Q2, Q3, Q4, Q5, Q6, Q7, Q8, Q9, Q10]), "operationType" : NewBodyOperationType.ADD, "oppositeDirection" : true, "depth" : 3.17 * mm, "offsetDistance" : 25.4 * mm});
        }
        {
            var Q0;
            Q0=makeQuery(id+"F14.imprint","IMPRINT",FACE,{"disambiguationData":[TD([[makeQuery(id+"F14.imprint","IMPRINT",EDGE,{"derivedFrom":sQuery(id+"F14.wireOp",EDGE,"E65.bottom")}),1.0]])]});
            var Q1;
            Q1=makeQuery(id+"F14.imprint","IMPRINT",FACE,{"disambiguationData":[TD([[makeQuery(id+"F14.imprint","IMPRINT",EDGE,{"derivedFrom":sQuery(id+"F14.wireOp",EDGE,"E68.bottom")}),-1.0]])]});
            var Q2;
            Q2=makeQuery(id+"F14.imprint","IMPRINT",FACE,{"disambiguationData":[TD([[makeQuery(id+"F14.imprint","IMPRINT",EDGE,{"derivedFrom":sQuery(id+"F14.wireOp",EDGE,"E65.bottom")}),-1.0]])]});
            var Q3;
            Q3=makeQuery(id+"F14.imprint","IMPRINT",FACE,{"disambiguationData":[TD([[makeQuery(id+"F14.imprint","IMPRINT",EDGE,{"derivedFrom":sQuery(id+"F14.wireOp",EDGE,"E67.top")}),-1.0]])]});
            var Q4;
            Q4=makeQuery(id+"F14.imprint","IMPRINT",FACE,{"disambiguationData":[TD([[makeQuery(id+"F14.imprint","IMPRINT",EDGE,{"derivedFrom":sQuery(id+"F14.wireOp",EDGE,"E67.bottom")}),-1.0]])]});
            var Q5;
            Q5=makeQuery(id+"F14.imprint","IMPRINT",FACE,{"disambiguationData":[TD([[makeQuery(id+"F14.imprint","IMPRINT",EDGE,{"derivedFrom":sQuery(id+"F14.wireOp",EDGE,"E66.right")}),-1.0]])]});
            var Q6;
            Q6=makeQuery(id+"F14.imprint","IMPRINT",FACE,{"disambiguationData":[TD([[makeQuery(id+"F14.imprint","IMPRINT",EDGE,{"derivedFrom":sQuery(id+"F14.wireOp",EDGE,"E66.bottom")}),-1.0]])]});
            var Q7;
            Q7=makeQuery(id+"F14.imprint","IMPRINT",FACE,{"disambiguationData":[TD([[makeQuery(id+"F14.imprint","IMPRINT",EDGE,{"derivedFrom":sQuery(id+"F14.wireOp",EDGE,"E65.top")}),-1.0]])]});
            extrude(context, id + "F16", {"entities" : qUnion([Q0, Q1, Q2, Q3, Q4, Q5, Q6, Q7]), "operationType" : NewBodyOperationType.ADD, "depth" : 17.46 * mm, "offsetDistance" : 25.4 * mm});
        }
        {
            var Q0;
            {var subQ0=sQuery(id+"F14.wireOp",EDGE,"E77");Q0=makeQuery(id+"F14.imprint","IMPRINT",FACE,{"disambiguationData":[TD([[makeQuery(id+"F14.imprint","IMPRINT",EDGE,{"derivedFrom":subQ0}),-1.0]])]});}
            extrude(context, id + "F17", {"entities" : qUnion([Q0]), "operationType" : NewBodyOperationType.ADD, "oppositeDirection" : true, "depth" : 3.17 * mm, "offsetDistance" : 25.4 * mm});
        }
        {
            var Q0;
            Q0=makeQuery(id+"F16.opExtrude","SWEPT_FACE",FACE,{"disambiguationData":[OSD([sQuery(id+"F14.wireOp",EDGE,"E65.left")])]});
            var sketch = newSketch(context, id + "F18", { "sketchPlane" : qUnion([Q0])});
            skCircle(sketch, "E101", {"center": v(-23.02, 122.63) * mm, "radius": 1.59 * mm});
            skCircle(sketch, "E102", {"center": v(-23.02, -190.9) * mm, "radius": 1.59 * mm});
            skCircle(sketch, "E103", {"center": v(-23.02, -86.5) * mm, "radius": 1.59 * mm});
            skCircle(sketch, "E104", {"center": v(-23.02, 18.24) * mm, "radius": 1.59 * mm});
            skLineSegment(sketch, "E105", {"start": v(-23.02, -190.9) * mm, "end": v(-23.02, -86.5) * mm, "construction": true});
            skLineSegment(sketch, "E106", {"start": v(-23.02, -86.5) * mm, "end": v(-23.02, 18.24) * mm, "construction": true});
            skLineSegment(sketch, "E107", {"start": v(-23.02, 18.24) * mm, "end": v(-23.02, 122.63) * mm, "construction": true});
            skLineSegment(sketch, "E108", {"start": v(-23.02, 122.63) * mm, "end": v(-23.4, 173.43) * mm, "construction": true});
            skSolve(sketch);
        }
        {
            var Q0;
            Q0 = qSketchRegion(id + "F18", true);
            extrude(context, id + "F19", {"entities" : qUnion([Q0]), "operationType" : NewBodyOperationType.REMOVE, "endBound" : BoundingType.THROUGH_ALL, "oppositeDirection" : true, "depth" : 762 * mm, "offsetDistance" : 25.4 * mm, "hasSecondDirection" : true, "secondDirectionOppositeDirection" : false, "secondDirectionDepth" : 762 * mm});
        }
        {
            var Q0;
            Q0=makeQuery(id+"F14.imprint","IMPRINT",FACE,{"disambiguationData":[TD([[makeQuery(id+"F14.imprint","IMPRINT",EDGE,{"derivedFrom":sQuery(id+"F14.wireOp",EDGE,"E70")}),1.0]])]});
            var Q1;
            Q1=makeQuery(id+"F14.imprint","IMPRINT",FACE,{"disambiguationData":[TD([[makeQuery(id+"F14.imprint","IMPRINT",EDGE,{"derivedFrom":sQuery(id+"F14.wireOp",EDGE,"E69")}),1.0]])]});
            var Q2;
            {var subQ0=sQuery(id+"F14.wireOp",EDGE,"E77");Q2=makeQuery(id+"F14.imprint","IMPRINT",FACE,{"disambiguationData":[TD([[makeQuery(id+"F14.imprint","IMPRINT",EDGE,{"derivedFrom":subQ0}),-1.0]])]});}
            var Q3;
            Q3=makeQuery(id+"F14.imprint","IMPRINT",FACE,{"disambiguationData":[TD([[makeQuery(id+"F14.imprint","IMPRINT",EDGE,{"derivedFrom":sQuery(id+"F14.wireOp",EDGE,"E79")}),-1.0]])]});
            var Q4;
            Q4=makeQuery(id+"F14.imprint","IMPRINT",FACE,{"disambiguationData":[TD([[makeQuery(id+"F14.imprint","IMPRINT",EDGE,{"derivedFrom":sQuery(id+"F14.wireOp",EDGE,"E89")}),-1.0]])]});
            var Q5;
            Q5=makeQuery(id+"F14.imprint","IMPRINT",FACE,{"disambiguationData":[TD([[makeQuery(id+"F14.imprint","IMPRINT",EDGE,{"derivedFrom":sQuery(id+"F14.wireOp",EDGE,"E90")}),-1.0]])]});
            var Q6;
            Q6=makeQuery(id+"F14.imprint","IMPRINT",FACE,{"disambiguationData":[TD([[makeQuery(id+"F14.imprint","IMPRINT",EDGE,{"derivedFrom":sQuery(id+"F14.wireOp",EDGE,"E83")}),-1.0]])]});
            var Q7;
            Q7=makeQuery(id+"F14.imprint","IMPRINT",FACE,{"disambiguationData":[TD([[makeQuery(id+"F14.imprint","IMPRINT",EDGE,{"derivedFrom":sQuery(id+"F14.wireOp",EDGE,"E84")}),-1.0]])]});
            extrude(context, id + "F20", {"entities" : qUnion([Q0, Q1, Q2, Q3, Q4, Q5, Q6, Q7]), "operationType" : NewBodyOperationType.REMOVE, "oppositeDirection" : true, "depth" : 25.4 * mm, "offsetDistance" : 25.4 * mm});
        }
    });
